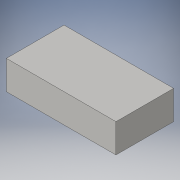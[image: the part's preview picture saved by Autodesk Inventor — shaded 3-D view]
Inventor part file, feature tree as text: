
AUTODESK INVENTOR PART (.ipt)
format: ipt  version: 2016 (Build 200138000, 138)  size: 82,944 bytes
history: native  units: in
note: dims shown in document units (in); Inventor stores cm internally (conversion verified against a paired STEP export)
features: extrude x1, sketch x1
ambient origin geometry x8: Origin, YZ Plane, XZ Plane, XY Plane, X Axis, Y Axis, Z Axis, Center Point
bodies: Solid1 (feature_tree)
feature tree (2):
  extrude  "Extrusion1"  Depth=0.7874in
  sketch  "Sketch1"  dims[d0=1.4961in d1=0.7874in d2=0.3937in d3=0.0in]
